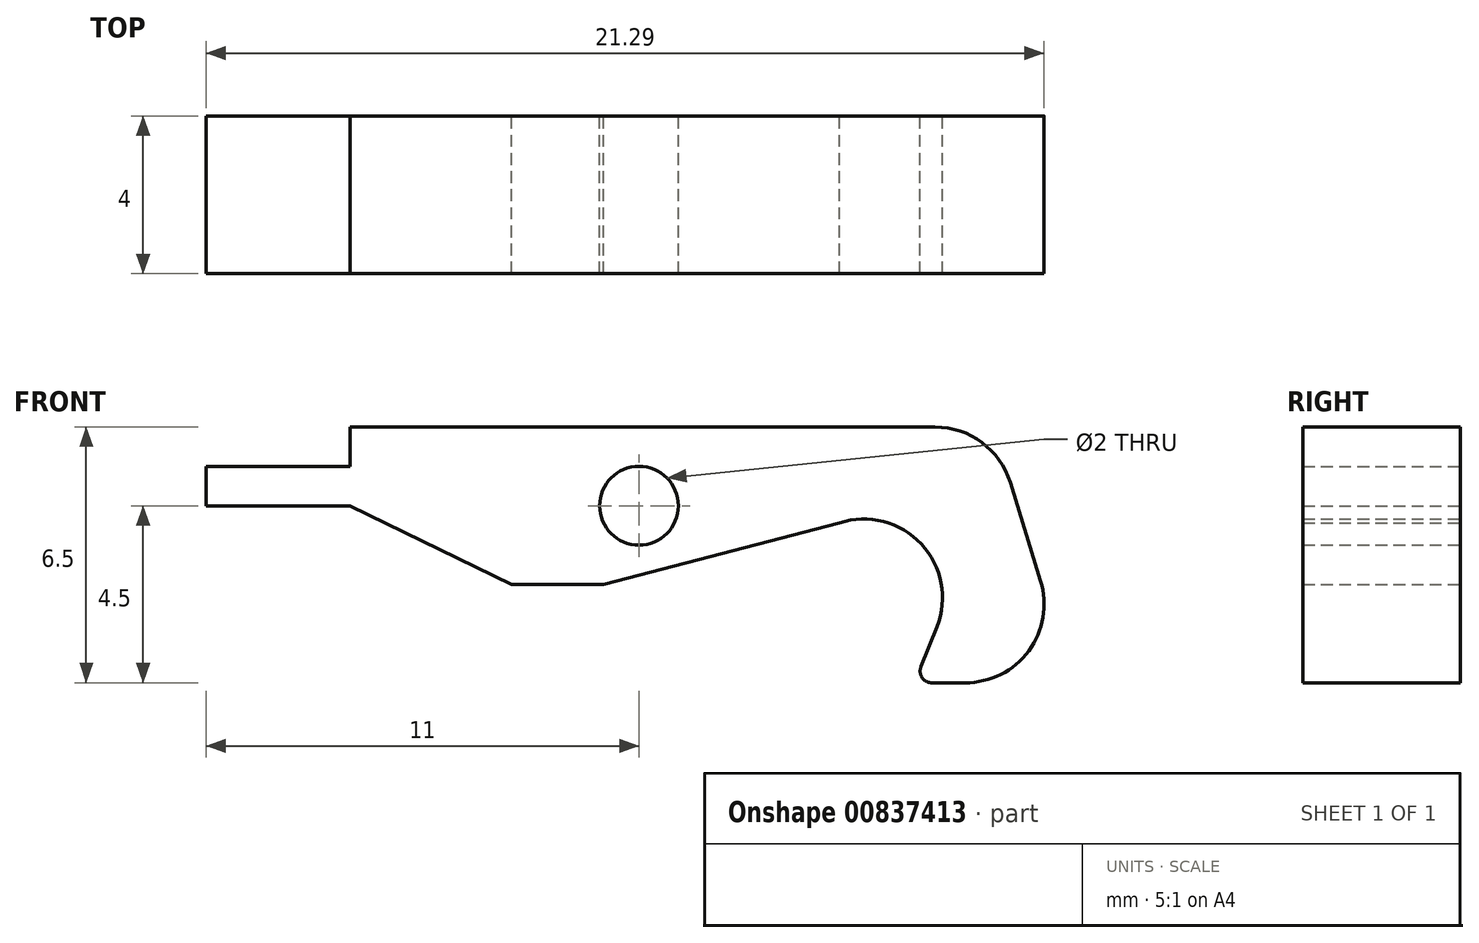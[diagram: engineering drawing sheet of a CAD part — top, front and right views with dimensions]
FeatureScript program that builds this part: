
annotation { "Feature Type Name" : "Feature", "Feature Type Description" : "" }
export const myFeature = defineFeature(function(context is Context, id is Id, definition is map)
    precondition{}
    {
        {
            var Q0;
            Q0=qCreatedBy(makeId("Front.planeOp"),FACE);
            var sketch = newSketch(context, id + "F0", { "sketchPlane" : qUnion([Q0])});
            skLineSegment(sketch, "E0", {"start": v(-7.34, 2) * mm, "end": v(7.52, 2) * mm});
            skLineSegment(sketch, "E1", {"start": v(9.43, 0.59) * mm, "end": v(10.2, -1.91) * mm});
            skLineSegment(sketch, "E2", {"start": v(8.3, -4.5) * mm, "end": v(7.44, -4.5) * mm});
            skLineSegment(sketch, "E3", {"start": v(7.16, -4.09) * mm, "end": v(7.57, -3.08) * mm});
            skLineSegment(sketch, "E4", {"start": v(-7.34, 0) * mm, "end": v(-11, 0) * mm});
            skLineSegment(sketch, "E5", {"start": v(-11, 0) * mm, "end": v(-11, 1) * mm});
            skPoint(sketch, "E6.orphan", {"position": v(-7.2, 2) * mm});
            skLineSegment(sketch, "E7", {"start": v(-7.34, 0) * mm, "end": v(-3.24, -2) * mm});
            skCircle(sketch, "E8", {"center": v(0, 0) * mm, "radius": 1 * mm});
            skPoint(sketch, "E9.visualSharp", {"position": v(8, -2) * mm});
            skPoint(sketch, "E10.visualSharp", {"position": v(9, 2) * mm});
            skArc(sketch, "E10.filletArc", {"start": v(9.43, 0.59) * mm, "mid": v(8.71, 1.6) * mm, "end": v(7.52, 2) * mm});
            skPoint(sketch, "E11.visualSharp", {"position": v(11, -4.5) * mm});
            skArc(sketch, "E11.filletArc", {"start": v(8.3, -4.5) * mm, "mid": v(9.9, -3.69) * mm, "end": v(10.2, -1.91) * mm});
            skPoint(sketch, "E12.visualSharp", {"position": v(7, -4.5) * mm});
            skArc(sketch, "E12.filletArc", {"start": v(7.16, -4.09) * mm, "mid": v(7.2, -4.37) * mm, "end": v(7.44, -4.5) * mm});
            skLineSegment(sketch, "E13", {"start": v(-11, 1) * mm, "end": v(-7.34, 1) * mm});
            skLineSegment(sketch, "E14", {"start": v(-7.34, 1) * mm, "end": v(-7.34, 2) * mm});
            skPoint(sketch, "E15.orphan", {"position": v(-11, 2) * mm});
            skPoint(sketch, "E16.visualSharp", {"position": v(4.23, 0) * mm});
            skPoint(sketch, "E17.visualSharp", {"position": v(6.8, 0) * mm});
            skPoint(sketch, "E18.visualSharp", {"position": v(9.15, 0.88) * mm});
            skArc(sketch, "E18.filletArc", {"start": v(7.57, -3.08) * mm, "mid": v(7.17, -0.97) * mm, "end": v(5.1, -0.44) * mm});
            skLineSegment(sketch, "E19", {"start": v(5.1, -0.44) * mm, "end": v(-0.9, -2) * mm});
            skLineSegment(sketch, "E20", {"start": v(-3.24, -2) * mm, "end": v(-0.9, -2) * mm});
            skSolve(sketch);
        }
        {
            var Q0;
            Q0 = qSketchRegion(id + "F0", true);
            extrude(context, id + "F1", {"entities" : qUnion([Q0]), "depth" : 2 * mm, "offsetDistance" : 25 * mm, "hasSecondDirection" : true, "secondDirectionOppositeDirection" : true, "secondDirectionDepth" : 2 * mm});
        }
    });
